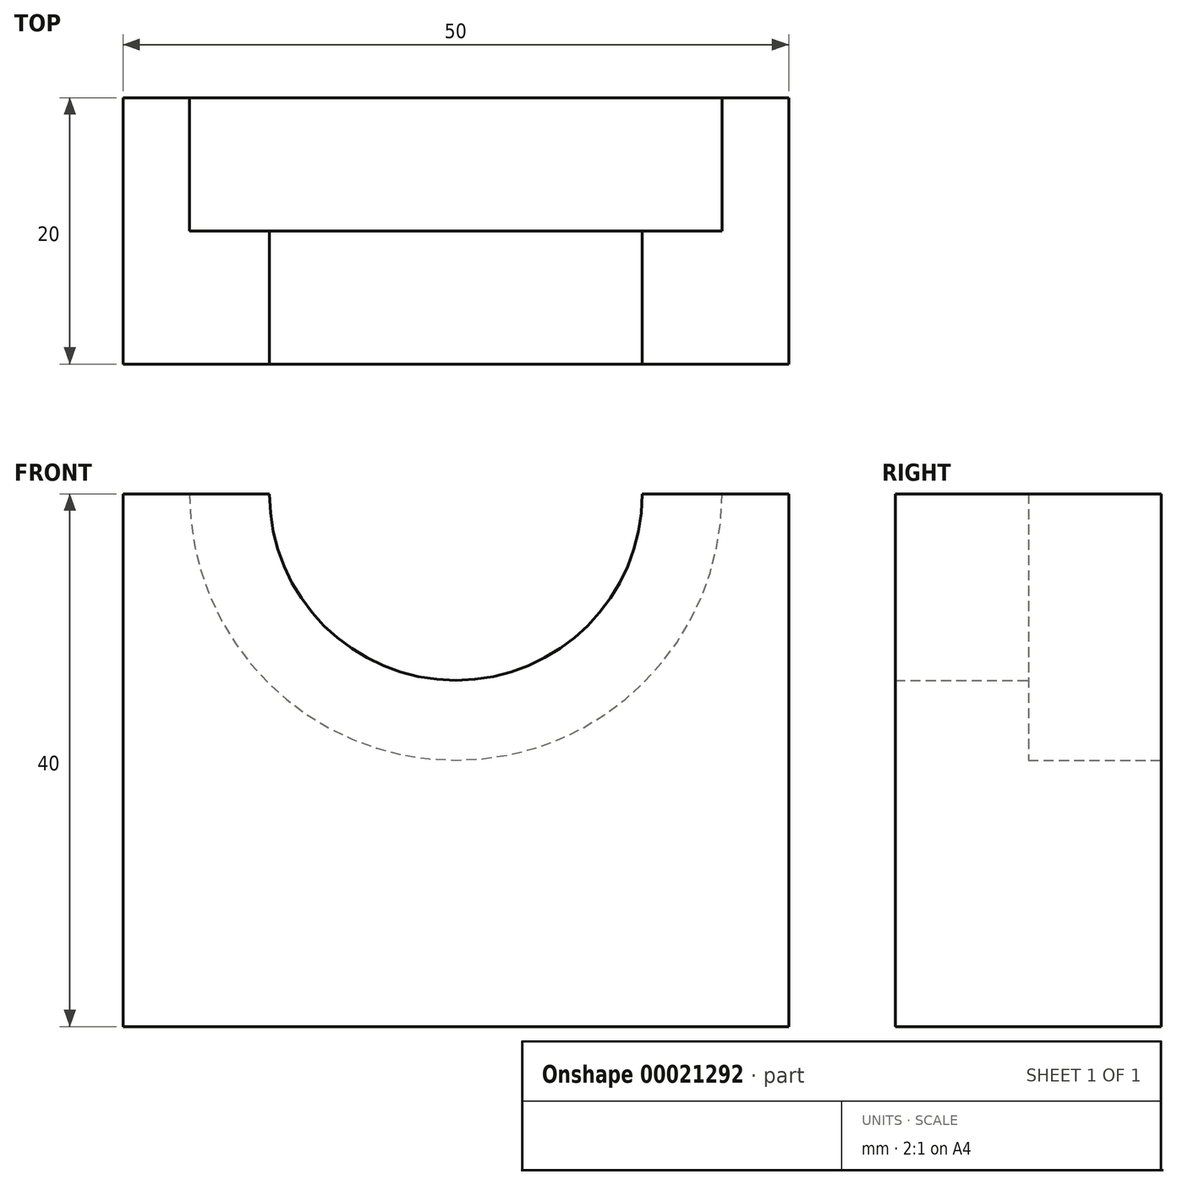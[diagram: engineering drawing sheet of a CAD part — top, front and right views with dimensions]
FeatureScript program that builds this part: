
annotation { "Feature Type Name" : "Feature", "Feature Type Description" : "" }
export const myFeature = defineFeature(function(context is Context, id is Id, definition is map)
    precondition{}
    {
        {
            var Q0;
            Q0=qCreatedBy(makeId("Top.planeOp"),FACE);
            var sketch = newSketch(context, id + "F0", { "sketchPlane" : qUnion([Q0])});
            skLineSegment(sketch, "E0.rect.bottom", {"start": v(25, -15) * mm, "end": v(-25, -15) * mm});
            skLineSegment(sketch, "E0.rect.top", {"start": v(25, 15) * mm, "end": v(-25, 15) * mm});
            skLineSegment(sketch, "E0.rect.left", {"start": v(25, -15) * mm, "end": v(25, 15) * mm});
            skLineSegment(sketch, "E0.rect.right", {"start": v(-25, -15) * mm, "end": v(-25, 15) * mm});
            skPoint(sketch, "E0.rect.middle", {"position": v(0, 0) * mm});
            skSolve(sketch);
        }
        {
            var Q0;
            Q0=makeQuery(id+"F0.imprint","IMPRINT",FACE,{"disambiguationData":[TD([[makeQuery(id+"F0.imprint","IMPRINT",EDGE,{"derivedFrom":sQuery(id+"F0.wireOp",EDGE,"E0.rect.bottom")}),-1.0]])]});
            extrude(context, id + "F1", {"entities" : qUnion([Q0]), "depth" : 40 * mm});
        }
        {
            var Q0;
            Q0=makeQuery(id+"F1.opExtrude","SWEPT_FACE",FACE,{"disambiguationData":[OSD([sQuery(id+"F0.wireOp",EDGE,"E0.rect.top")])]});
            var sketch = newSketch(context, id + "F2", { "sketchPlane" : qUnion([Q0])});
            skArc(sketch, "E1", {"start": v(-20, 40) * mm, "mid": v(0, 20) * mm, "end": v(20, 40) * mm});
            skLineSegment(sketch, "E2", {"start": v(-20, 40) * mm, "end": v(20, 40) * mm});
            skSolve(sketch);
        }
        {
            var Q0;
            Q0 = qSketchRegion(id + "F2", true);
            extrude(context, id + "F3", {"entities" : qUnion([Q0]), "operationType" : NewBodyOperationType.REMOVE, "oppositeDirection" : true, "depth" : 20 * mm});
        }
        {
            var Q0;
            Q0=makeQuery(id+"F3.boolean.opBoolean","COPY",FACE,{"derivedFrom":makeQuery(id+"F3.opExtrude","CAP_FACE",FACE,{"disambiguationData":[OSD([sQuery(id+"F2.wireOp",EDGE,"E1"),sQuery(id+"F2.wireOp",EDGE,"E2")])],"isStart":false})});
            var sketch = newSketch(context, id + "F4", { "sketchPlane" : qUnion([Q0])});
            skArc(sketch, "E3", {"start": v(-14, 40) * mm, "mid": v(0, 26) * mm, "end": v(14, 40) * mm});
            skLineSegment(sketch, "E4", {"start": v(-14, 40) * mm, "end": v(14, 40) * mm});
            skSolve(sketch);
        }
        {
            var Q0;
            Q0 = qSketchRegion(id + "F4", true);
            var Q1;
            Q1=makeQuery(id+"F1.opExtrude","SWEPT_FACE",FACE,{"disambiguationData":[OSD([sQuery(id+"F0.wireOp",EDGE,"E0.rect.bottom")])]});
            extrude(context, id + "F5", {"entities" : qUnion([Q0]), "operationType" : NewBodyOperationType.REMOVE, "endBound" : BoundingType.UP_TO_SURFACE, "oppositeDirection" : true, "endBoundEntityFace" : qUnion([Q1]), "depth" : 25 * mm});
        }
        {
            var Q0;
            Q0=makeQuery(id+"F1.opExtrude","SWEPT_FACE",FACE,{"disambiguationData":[OSD([sQuery(id+"F0.wireOp",EDGE,"E0.rect.top")])]});
            cPlane(context, id + "F6", {"entities" : qUnion([Q0]), "cplaneType" : CPlaneType.OFFSET, "offset" : 10 * mm, "oppositeDirection" : true, "width" : 150 * mm, "height" : 150 * mm});
        }
        {
            var Q0;
            Q0=makeQuery(id+"F1.opExtrude","SWEPT_FACE",FACE,{"disambiguationData":[OSD([sQuery(id+"F0.wireOp",EDGE,"E0.rect.top")])]});
            var Q1;
            Q1=qCreatedBy(id+"F6.planeOp",FACE);
            extrude(context, id + "F7", {"entities" : qUnion([Q0]), "operationType" : NewBodyOperationType.REMOVE, "endBound" : BoundingType.UP_TO_SURFACE, "oppositeDirection" : true, "endBoundEntityFace" : qUnion([Q1]), "depth" : 25 * mm});
        }
    });
